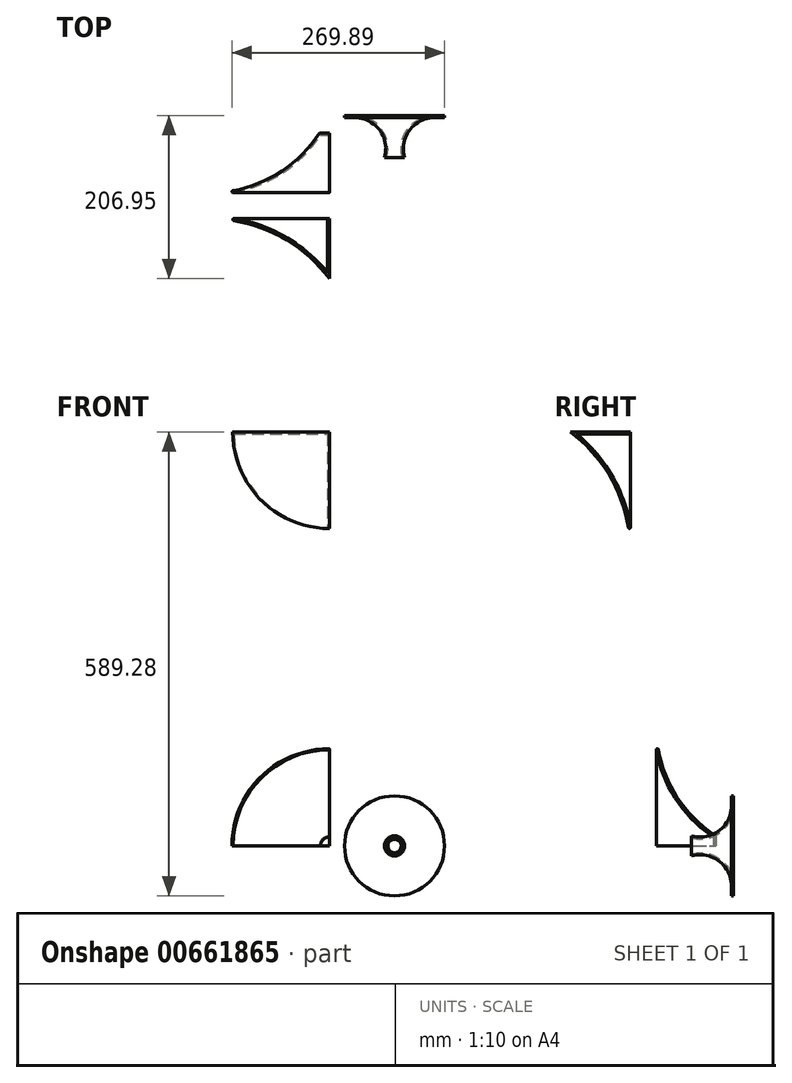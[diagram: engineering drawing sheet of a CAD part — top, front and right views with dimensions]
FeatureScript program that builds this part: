
annotation { "Feature Type Name" : "Feature", "Feature Type Description" : "" }
export const myFeature = defineFeature(function(context is Context, id is Id, definition is map)
    precondition{}
    {
        {
            var Q0;
            Q0=qCreatedBy(makeId("Top.planeOp"),FACE);
            var sketch = newSketch(context, id + "F0", { "sketchPlane" : qUnion([Q0])});
            skArc(sketch, "E0", {"start": v(-151.14, 0) * mm, "mid": v(-72.24, 20.12) * mm, "end": v(-12.6, 75.57) * mm});
            skLineSegment(sketch, "E1", {"start": v(0, 0) * mm, "end": v(-151.14, 0) * mm});
            skLineSegment(sketch, "E2", {"start": v(0, -32.86) * mm, "end": v(0, -109.06) * mm});
            skLineSegment(sketch, "E3", {"start": v(0, -32.86) * mm, "end": v(-152.4, -32.86) * mm});
            skArc(sketch, "E4", {"start": v(0, -109.06) * mm, "mid": v(-67.2, -52.97) * mm, "end": v(-152.4, -32.86) * mm});
            skLineSegment(sketch, "E5", {"start": v(-12.6, 75.57) * mm, "end": v(0, 75.57) * mm});
            skLineSegment(sketch, "E6", {"start": v(82.9, 44.55) * mm, "end": v(82.9, 95.35) * mm});
            skLineSegment(sketch, "E7", {"start": v(82.9, 44.55) * mm, "end": v(70.2, 44.55) * mm});
            skArc(sketch, "E8", {"start": v(70.2, 44.55) * mm, "mid": v(63.85, 79.47) * mm, "end": v(32.1, 95.35) * mm});
            skPoint(sketch, "E9.end.orphan", {"position": v(0, 125.95) * mm});
            skLineSegment(sketch, "E10", {"start": v(0, 0) * mm, "end": v(0, 75.57) * mm});
            skLineSegment(sketch, "E11", {"start": v(32.1, 95.35) * mm, "end": v(19.4, 95.35) * mm});
            skLineSegment(sketch, "E12", {"start": v(82.9, 95.35) * mm, "end": v(82.9, 108.05) * mm});
            skLineSegment(sketch, "E13", {"start": v(19.4, 95.35) * mm, "end": v(19.4, 108.05) * mm});
            skLineSegment(sketch, "E14", {"start": v(82.9, 108.05) * mm, "end": v(19.4, 108.05) * mm});
            skSolve(sketch);
        }
        {
            var Q0;
            Q0=makeQuery(id+"F0.imprint","IMPRINT",FACE,{"disambiguationData":[TD([[makeQuery(id+"F0.imprint","IMPRINT",EDGE,{"derivedFrom":sQuery(id+"F0.wireOp",EDGE,"E0")}),-1.0]])]});
            var Q1;
            Q1=sQuery(id+"F0.wireOp",EDGE,"E10");
            revolve(context, id + "F1", {"entities" : qUnion([Q0]), "axis" : qUnion([Q1]), "revolveType" : RevolveType.ONE_DIRECTION, "angle" : 90 * degree});
        }
        {
            var Q0;
            Q0=makeQuery(id+"F0.imprint","IMPRINT",FACE,{"disambiguationData":[TD([[makeQuery(id+"F0.imprint","IMPRINT",EDGE,{"derivedFrom":sQuery(id+"F0.wireOp",EDGE,"E2")}),-1.0]])]});
            var Q1;
            Q1=sQuery(id+"F0.wireOp",EDGE,"E2");
            revolve(context, id + "F2", {"entities" : qUnion([Q0]), "axis" : qUnion([Q1]), "revolveType" : RevolveType.ONE_DIRECTION, "angle" : 90 * degree});
        }
        {
            var Q0;
            Q0=makeQuery(id+"F1.opRevolve","SWEPT_FACE",FACE,{"disambiguationData":[OSD([sQuery(id+"F0.wireOp",EDGE,"E1")])]});
            var Q1;
            Q1=makeQuery(id+"F2.opRevolve","SWEPT_FACE",FACE,{"disambiguationData":[OSD([sQuery(id+"F0.wireOp",EDGE,"E3")])]});
            var Q2;
            Q2=makeQuery(id+"F1.opRevolve","SWEPT_FACE",FACE,{"disambiguationData":[OSD([sQuery(id+"F0.wireOp",EDGE,"hsk4Ko9h-fMbb-4g5f-9Kgs-6Lf86D6iJKgB")])]});
            var Q3;
            Q3=makeQuery(id+"F1.opRevolve","CAP_FACE",FACE,{"disambiguationData":[OSD([sQuery(id+"F0.wireOp",EDGE,"E0"),sQuery(id+"F0.wireOp",EDGE,"AliqaOaG-pH27-VV7b-wARR-vgf4CyrOY9jt"),sQuery(id+"F0.wireOp",EDGE,"hsk4Ko9h-fMbb-4g5f-9Kgs-6Lf86D6iJKgB"),sQuery(id+"F0.wireOp",EDGE,"E1"),sQuery(id+"F0.wireOp",EDGE,"E9")])],"isStart":false});
            var Q4;
            Q4=makeQuery(id+"F1.opRevolve","CAP_FACE",FACE,{"disambiguationData":[OSD([sQuery(id+"F0.wireOp",EDGE,"E0"),sQuery(id+"F0.wireOp",EDGE,"AliqaOaG-pH27-VV7b-wARR-vgf4CyrOY9jt"),sQuery(id+"F0.wireOp",EDGE,"hsk4Ko9h-fMbb-4g5f-9Kgs-6Lf86D6iJKgB"),sQuery(id+"F0.wireOp",EDGE,"E1"),sQuery(id+"F0.wireOp",EDGE,"E9")])],"isStart":true});
            shell(context, id + "F3", {"entities" : qUnion([Q0, Q1, Q2, Q3, Q4]), "thickness" : 2.54 * mm});
        }
        {
            var Q0;
            Q0=makeQuery(id+"F2.opRevolve","SWEPT_BODY",BODY,{"disambiguationData":[OSD([sQuery(id+"F0.wireOp",EDGE,"E2"),sQuery(id+"F0.wireOp",EDGE,"E3"),sQuery(id+"F0.wireOp",EDGE,"E4")])]});
            var Q1;
            Q1=makeQuery(id+"F2.opRevolve","SWEPT_EDGE",EDGE,{"disambiguationData":[OSD([sQuery(id+"F0.wireOp",EDGE,"E3"),sQuery(id+"F0.wireOp",EDGE,"E4")])]});
            transform(context, id + "F4", {"entities" : qUnion([Q0]), "transformType" : TransformType.TRANSLATION_3D, "dx" : 0 * mm, "dy" : 0 * mm, "dz" : 525.78 * mm, "makeCopy" : false});
        }
        {
            var Q0;
            Q0=makeQuery(id+"F1.opRevolve","SWEPT_EDGE",EDGE,{"disambiguationData":[OSD([sQuery(id+"F0.wireOp",EDGE,"E0"),sQuery(id+"F0.wireOp",EDGE,"E1")])]});
            var Q1;
            Q1=makeQuery(id+"F2.opRevolve","SWEPT_EDGE",EDGE,{"disambiguationData":[OSD([sQuery(id+"F0.wireOp",EDGE,"E3"),sQuery(id+"F0.wireOp",EDGE,"E4")])]});
            fillet(context, id + "F5", {"entities" : qUnion([Q0, Q1]), "radius" : 1.27 * mm, "tangentPropagation" : true, "allowEdgeOverflow" : false});
        }
        {
            var Q0;
            {var subQ0=sQuery(id+"F0.wireOp",EDGE,"E4");var subQ1=sQuery(id+"F0.wireOp",EDGE,"E3");var subQ2=sQuery(id+"F0.wireOp",EDGE,"E2");Q0=makeQuery(id+"F3.opShell","OFFSET_FACE",FACE,{"disambiguationData":[OSD([subQ2,subQ1,subQ0]),TDD([makeQuery(id+"F2.opRevolve","CAP_FACE",FACE,{"disambiguationData":[OSD([subQ2,subQ1,subQ0])],"isStart":true})])]});}
            extrude(context, id + "F6", {"entities" : qUnion([Q0]), "operationType" : NewBodyOperationType.REMOVE, "oppositeDirection" : true, "depth" : 25.4 * mm, "offsetDistance" : 25.4 * mm});
        }
        {
            var Q0;
            {var subQ0=sQuery(id+"F0.wireOp",EDGE,"E2");var subQ1=sQuery(id+"F0.wireOp",EDGE,"E4");var subQ2=sQuery(id+"F0.wireOp",EDGE,"E3");Q0=makeQuery(id+"F6.boolean.opBoolean","MERGE",FACE,{"derivedFrom":[makeQuery(id+"F3.opShell","OFFSET_FACE",FACE,{"disambiguationData":[OSD([subQ0,subQ2,subQ1]),TDD([makeQuery(id+"F2.opRevolve","CAP_FACE",FACE,{"disambiguationData":[OSD([subQ0,subQ2,subQ1])],"isStart":false})])]}),makeQuery(id+"F6.opExtrude","SWEPT_FACE",FACE,{"disambiguationData":[OSD([subQ0])]})]});}
            extrude(context, id + "F7", {"entities" : qUnion([Q0]), "operationType" : NewBodyOperationType.REMOVE, "oppositeDirection" : true, "depth" : 25.4 * mm, "offsetDistance" : 25.4 * mm});
        }
        {
            var Q0;
            Q0=makeQuery(id+"F0.imprint","IMPRINT",FACE,{"disambiguationData":[TD([[makeQuery(id+"F0.imprint","IMPRINT",EDGE,{"derivedFrom":sQuery(id+"F0.wireOp",EDGE,"E6")}),1.0]])]});
            var Q1;
            Q1=sQuery(id+"F0.wireOp",EDGE,"E6");
            revolve(context, id + "F8", {"entities" : qUnion([Q0]), "axis" : qUnion([Q1]), "revolveType" : RevolveType.FULL});
        }
        {
            var Q0;
            Q0=makeQuery(id+"F8.opRevolve","SWEPT_FACE",FACE,{"disambiguationData":[OSD([sQuery(id+"F0.wireOp",EDGE,"E14")])]});
            var Q1;
            Q1=makeQuery(id+"F8.opRevolve","SWEPT_FACE",FACE,{"disambiguationData":[OSD([sQuery(id+"F0.wireOp",EDGE,"E7")])]});
            shell(context, id + "F9", {"entities" : qUnion([Q0, Q1]), "thickness" : 2.54 * mm});
        }
        {
            var Q0;
            Q0=makeQuery(id+"F8.opRevolve","SWEPT_FACE",FACE,{"disambiguationData":[OSD([sQuery(id+"F0.wireOp",EDGE,"E14")])]});
            extrude(context, id + "F10", {"entities" : qUnion([Q0]), "operationType" : NewBodyOperationType.REMOVE, "oppositeDirection" : true, "depth" : 10.16 * mm, "offsetDistance" : 25.4 * mm});
        }
    });
